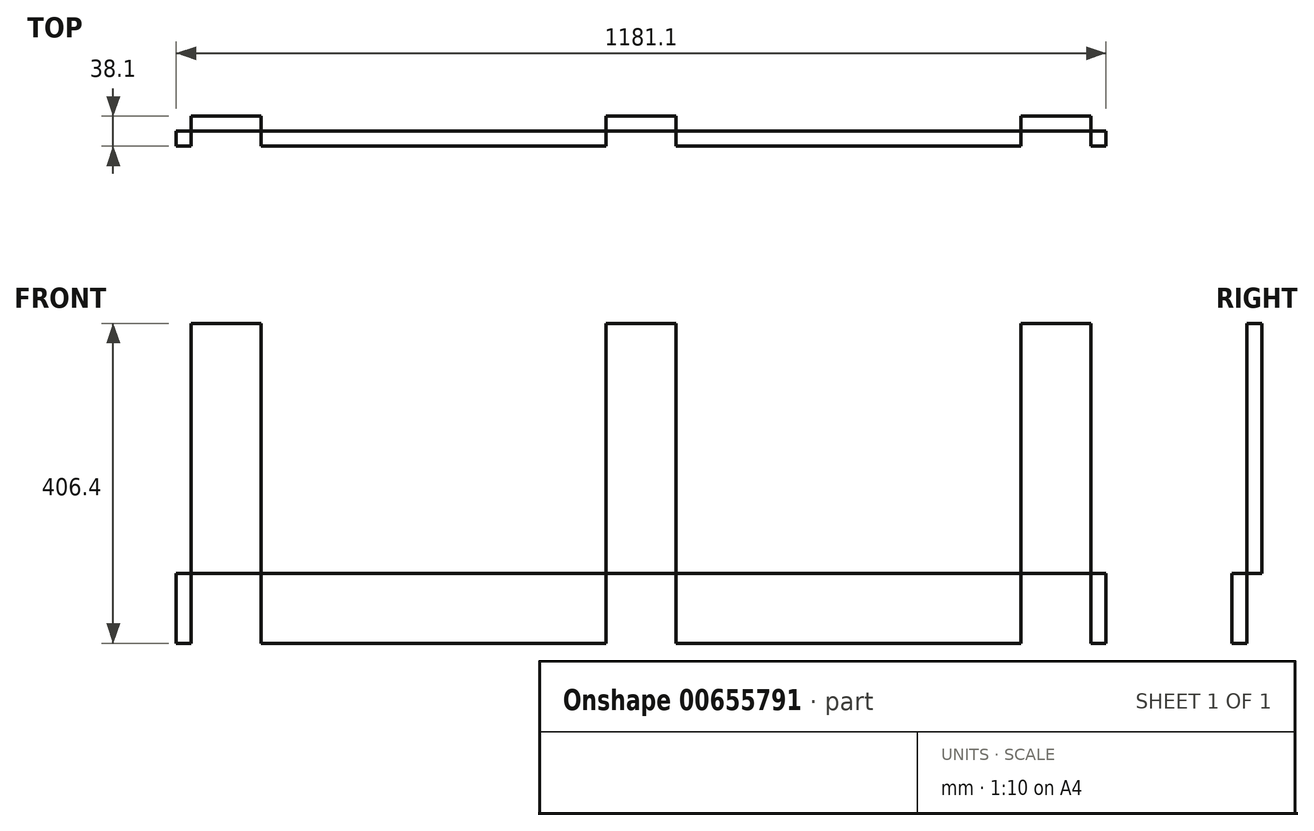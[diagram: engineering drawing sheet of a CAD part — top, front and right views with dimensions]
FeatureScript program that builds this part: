
annotation { "Feature Type Name" : "Feature", "Feature Type Description" : "" }
export const myFeature = defineFeature(function(context is Context, id is Id, definition is map)
    precondition{}
    {
        {
            var Q0;
            Q0=qCreatedBy(makeId("Front.planeOp"),FACE);
            var sketch = newSketch(context, id + "F0", { "sketchPlane" : qUnion([Q0])});
            skLineSegment(sketch, "E0.bottom", {"start": v(590.55, 44.45) * mm, "end": v(-590.55, 44.45) * mm});
            skLineSegment(sketch, "E0.top", {"start": v(590.55, -44.45) * mm, "end": v(-590.55, -44.45) * mm});
            skLineSegment(sketch, "E0.left", {"start": v(590.55, 44.45) * mm, "end": v(590.55, -44.45) * mm});
            skLineSegment(sketch, "E0.right", {"start": v(-590.55, 44.45) * mm, "end": v(-590.55, -44.45) * mm});
            skPoint(sketch, "E0.middle", {"position": v(0, 0) * mm});
            skLineSegment(sketch, "E1.bottom", {"start": v(571.5, -44.45) * mm, "end": v(482.6, -44.45) * mm});
            skLineSegment(sketch, "E1.top", {"start": v(571.5, 361.95) * mm, "end": v(482.6, 361.95) * mm});
            skLineSegment(sketch, "E1.left", {"start": v(571.5, -44.45) * mm, "end": v(571.5, 361.95) * mm});
            skLineSegment(sketch, "E1.right", {"start": v(482.6, -44.45) * mm, "end": v(482.6, 361.95) * mm});
            skLineSegment(sketch, "E2.bottom", {"start": v(44.45, -44.45) * mm, "end": v(-44.45, -44.45) * mm});
            skLineSegment(sketch, "E2.top", {"start": v(44.45, 361.95) * mm, "end": v(-44.45, 361.95) * mm});
            skLineSegment(sketch, "E2.left", {"start": v(44.45, -44.45) * mm, "end": v(44.45, 361.95) * mm});
            skLineSegment(sketch, "E2.right", {"start": v(-44.45, -44.45) * mm, "end": v(-44.45, 361.95) * mm});
            skLineSegment(sketch, "E3.bottom", {"start": v(-571.5, -44.45) * mm, "end": v(-482.6, -44.45) * mm});
            skLineSegment(sketch, "E3.top", {"start": v(-571.5, 361.95) * mm, "end": v(-482.6, 361.95) * mm});
            skLineSegment(sketch, "E3.left", {"start": v(-571.5, -44.45) * mm, "end": v(-571.5, 361.95) * mm});
            skLineSegment(sketch, "E3.right", {"start": v(-482.6, -44.45) * mm, "end": v(-482.6, 361.95) * mm});
            skSolve(sketch);
        }
        {
            var Q0;
            {var subQ5=sQuery(id+"F0.wireOp",EDGE,"E3.bottom");Q0=makeQuery(id+"F0.imprint","IMPRINT",FACE,{"disambiguationData":[TD([[makeQuery(id+"F0.imprint","IMPRINT",EDGE,{"derivedFrom":subQ5}),1.0]])]});}
            var Q1;
            {var subQ5=sQuery(id+"F0.wireOp",EDGE,"E3.top");Q1=makeQuery(id+"F0.imprint","IMPRINT",FACE,{"disambiguationData":[TD([[makeQuery(id+"F0.imprint","IMPRINT",EDGE,{"derivedFrom":subQ5}),-1.0]])]});}
            var Q2;
            {var subQ5=sQuery(id+"F0.wireOp",EDGE,"E2.bottom");Q2=makeQuery(id+"F0.imprint","IMPRINT",FACE,{"disambiguationData":[TD([[makeQuery(id+"F0.imprint","IMPRINT",EDGE,{"derivedFrom":subQ5}),-1.0]])]});}
            var Q3;
            {var subQ5=sQuery(id+"F0.wireOp",EDGE,"E2.top");Q3=makeQuery(id+"F0.imprint","IMPRINT",FACE,{"disambiguationData":[TD([[makeQuery(id+"F0.imprint","IMPRINT",EDGE,{"derivedFrom":subQ5}),1.0]])]});}
            var Q4;
            {var subQ5=sQuery(id+"F0.wireOp",EDGE,"E1.bottom");Q4=makeQuery(id+"F0.imprint","IMPRINT",FACE,{"disambiguationData":[TD([[makeQuery(id+"F0.imprint","IMPRINT",EDGE,{"derivedFrom":subQ5}),-1.0]])]});}
            var Q5;
            {var subQ5=sQuery(id+"F0.wireOp",EDGE,"E1.top");Q5=makeQuery(id+"F0.imprint","IMPRINT",FACE,{"disambiguationData":[TD([[makeQuery(id+"F0.imprint","IMPRINT",EDGE,{"derivedFrom":subQ5}),1.0]])]});}
            extrude(context, id + "F1", {"entities" : qUnion([Q0, Q1, Q2, Q3, Q4, Q5]), "oppositeDirection" : true, "depth" : 19.05 * mm, "offsetDistance" : 19.05 * mm});
        }
        {
            var Q0;
            {var subQ0=sQuery(id+"F0.wireOp",EDGE,"E2.right");var subQ1=sQuery(id+"F0.wireOp",EDGE,"E0.bottom");var subQ2=makeQuery(id+"F0.imprint","INTERSECT",VERTEX,{"derivedFrom":[subQ1,subQ0]});Q0=makeQuery(id+"F0.imprint","IMPRINT",FACE,{"disambiguationData":[TD([[makeQuery(id+"F0.imprint","IMPRINT",EDGE,{"disambiguationData":[TD([[subQ2,-1.0]])],"derivedFrom":subQ1}),1.0]])]});}
            var Q1;
            {var subQ5=sQuery(id+"F0.wireOp",EDGE,"E3.bottom");Q1=makeQuery(id+"F0.imprint","IMPRINT",FACE,{"disambiguationData":[TD([[makeQuery(id+"F0.imprint","IMPRINT",EDGE,{"derivedFrom":subQ5}),1.0]])]});}
            var Q2;
            {var subQ0=sQuery(id+"F0.wireOp",EDGE,"E0.right");Q2=makeQuery(id+"F0.imprint","IMPRINT",FACE,{"disambiguationData":[TD([[makeQuery(id+"F0.imprint","IMPRINT",EDGE,{"derivedFrom":subQ0}),1.0]])]});}
            var Q3;
            {var subQ5=sQuery(id+"F0.wireOp",EDGE,"E2.bottom");Q3=makeQuery(id+"F0.imprint","IMPRINT",FACE,{"disambiguationData":[TD([[makeQuery(id+"F0.imprint","IMPRINT",EDGE,{"derivedFrom":subQ5}),-1.0]])]});}
            var Q4;
            {var subQ0=sQuery(id+"F0.wireOp",EDGE,"E1.right");var subQ1=sQuery(id+"F0.wireOp",EDGE,"E0.bottom");var subQ2=makeQuery(id+"F0.imprint","INTERSECT",VERTEX,{"derivedFrom":[subQ1,subQ0]});Q4=makeQuery(id+"F0.imprint","IMPRINT",FACE,{"disambiguationData":[TD([[makeQuery(id+"F0.imprint","IMPRINT",EDGE,{"disambiguationData":[TD([[subQ2,-1.0]])],"derivedFrom":subQ1}),1.0]])]});}
            var Q5;
            {var subQ5=sQuery(id+"F0.wireOp",EDGE,"E1.bottom");Q5=makeQuery(id+"F0.imprint","IMPRINT",FACE,{"disambiguationData":[TD([[makeQuery(id+"F0.imprint","IMPRINT",EDGE,{"derivedFrom":subQ5}),-1.0]])]});}
            var Q6;
            {var subQ0=sQuery(id+"F0.wireOp",EDGE,"E0.left");Q6=makeQuery(id+"F0.imprint","IMPRINT",FACE,{"disambiguationData":[TD([[makeQuery(id+"F0.imprint","IMPRINT",EDGE,{"derivedFrom":subQ0}),-1.0]])]});}
            extrude(context, id + "F2", {"entities" : qUnion([Q0, Q1, Q2, Q3, Q4, Q5, Q6]), "depth" : 19.05 * mm, "offsetDistance" : 25.4 * mm});
        }
    });
